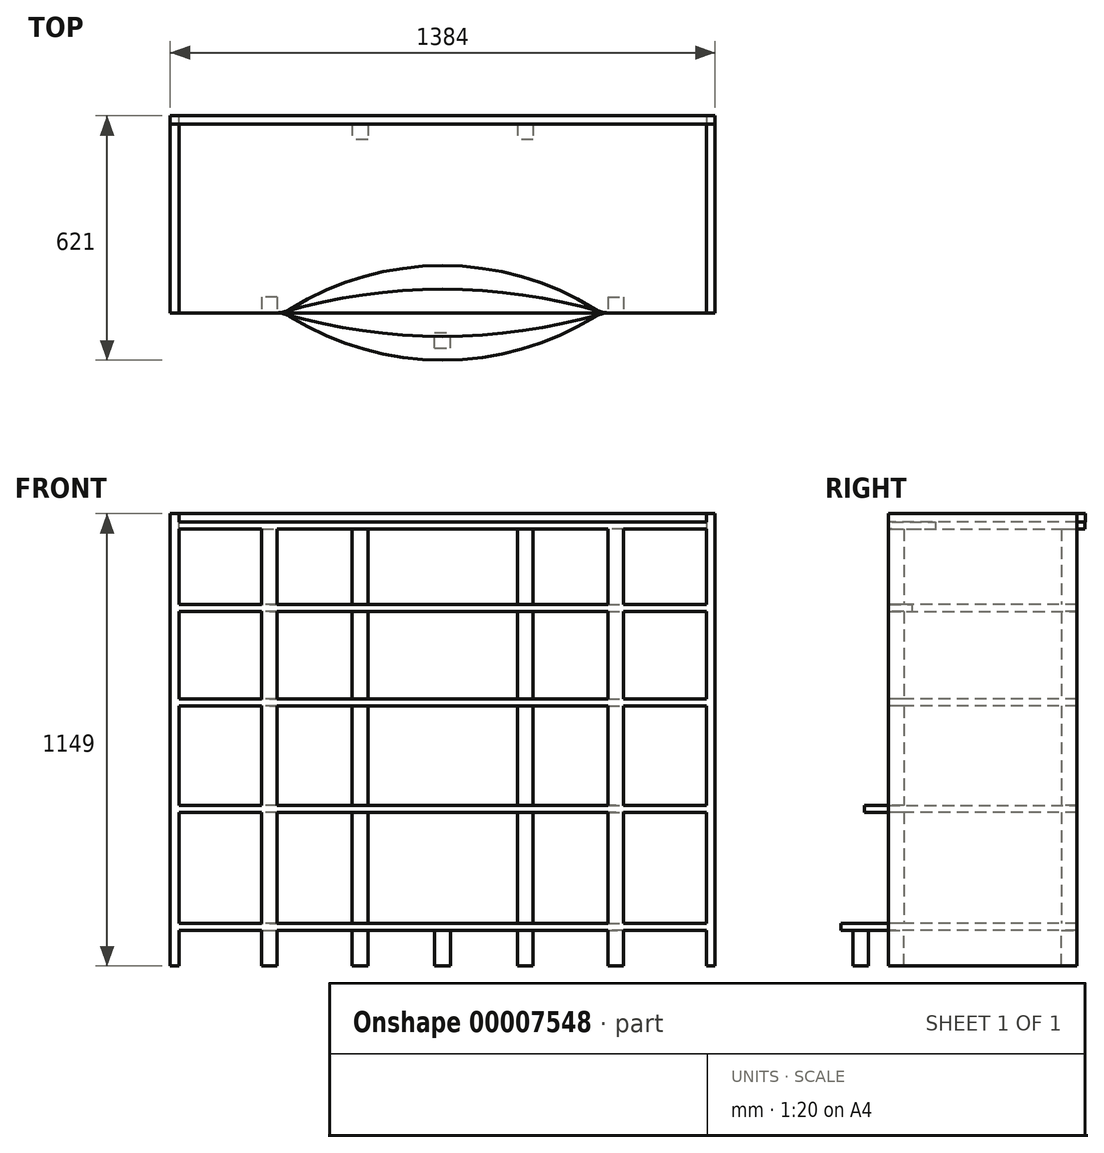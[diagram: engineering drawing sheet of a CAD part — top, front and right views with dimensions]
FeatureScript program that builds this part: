
annotation { "Feature Type Name" : "Feature", "Feature Type Description" : "" }
export const myFeature = defineFeature(function(context is Context, id is Id, definition is map)
    precondition{}
    {
        {
            var Q0;
            Q0=qCreatedBy(makeId("Top.planeOp"),FACE);
            var sketch = newSketch(context, id + "F0", { "sketchPlane" : qUnion([Q0])});
            skLineSegment(sketch, "E0", {"start": v(-670, 0) * mm, "end": v(-670, -480) * mm});
            skLineSegment(sketch, "E1", {"start": v(-670, -480) * mm, "end": v(-420, -480) * mm});
            skLineSegment(sketch, "E2", {"start": v(-670, 0) * mm, "end": v(670, 0) * mm});
            skLineSegment(sketch, "E3", {"start": v(670, 0) * mm, "end": v(670, -480) * mm});
            skLineSegment(sketch, "E4", {"start": v(670, -480) * mm, "end": v(420, -480) * mm});
            skArc(sketch, "E5", {"start": v(-388.3, -489.06) * mm, "mid": v(0, -600) * mm, "end": v(388.3, -489.06) * mm});
            skPoint(sketch, "E6.visualSharp", {"position": v(-402.5, -480) * mm});
            skArc(sketch, "E6.filletArc", {"start": v(-388.3, -489.06) * mm, "mid": v(-403.52, -482.3) * mm, "end": v(-420, -480) * mm});
            skPoint(sketch, "E7.visualSharp", {"position": v(402.5, -480) * mm});
            skArc(sketch, "E7.filletArc", {"start": v(420, -480) * mm, "mid": v(403.52, -482.3) * mm, "end": v(388.3, -489.06) * mm});
            skSolve(sketch);
        }
        {
            var Q0;
            Q0=qCreatedBy(makeId("Top.planeOp"),FACE);
            cPlane(context, id + "F1", {"entities" : qUnion([Q0]), "cplaneType" : CPlaneType.OFFSET, "offset" : 300 * mm, "width" : 150 * mm, "height" : 150 * mm});
        }
        {
            var Q0;
            Q0=qCreatedBy(id+"F1.planeOp",FACE);
            var sketch = newSketch(context, id + "F2", { "sketchPlane" : qUnion([Q0])});
            skLineSegment(sketch, "E8", {"start": v(-670, 0) * mm, "end": v(-670, -480) * mm});
            skLineSegment(sketch, "E9", {"start": v(-670, -480) * mm, "end": v(-420, -480) * mm});
            skLineSegment(sketch, "E10", {"start": v(420, -480) * mm, "end": v(670, -480) * mm});
            skLineSegment(sketch, "E11", {"start": v(670, -480) * mm, "end": v(670, 0) * mm});
            skLineSegment(sketch, "E12", {"start": v(670, 0) * mm, "end": v(-670, 0) * mm});
            skArc(sketch, "E13", {"start": v(-403.2, -482.4) * mm, "mid": v(0, -540) * mm, "end": v(403.2, -482.4) * mm});
            skPoint(sketch, "E14.visualSharp", {"position": v(-411.34, -480) * mm});
            skArc(sketch, "E14.filletArc", {"start": v(-403.2, -482.4) * mm, "mid": v(-411.51, -480.6) * mm, "end": v(-420, -480) * mm});
            skPoint(sketch, "E15.visualSharp", {"position": v(411.34, -480) * mm});
            skArc(sketch, "E15.filletArc", {"start": v(420, -480) * mm, "mid": v(411.51, -480.6) * mm, "end": v(403.2, -482.4) * mm});
            skSolve(sketch);
        }
        {
            var Q0;
            Q0=qCreatedBy(id+"F1.planeOp",FACE);
            cPlane(context, id + "F3", {"entities" : qUnion([Q0]), "cplaneType" : CPlaneType.OFFSET, "offset" : 270 * mm, "width" : 150 * mm, "height" : 150 * mm});
        }
        {
            var Q0;
            Q0=qCreatedBy(id+"F3.planeOp",FACE);
            var sketch = newSketch(context, id + "F4", { "sketchPlane" : qUnion([Q0])});
            skLineSegment(sketch, "E16.bottom", {"start": v(-670, 0) * mm, "end": v(670, 0) * mm});
            skLineSegment(sketch, "E16.top", {"start": v(-670, -480) * mm, "end": v(670, -480) * mm});
            skLineSegment(sketch, "E16.left", {"start": v(-670, 0) * mm, "end": v(-670, -480) * mm});
            skLineSegment(sketch, "E16.right", {"start": v(670, 0) * mm, "end": v(670, -480) * mm});
            skSolve(sketch);
        }
        {
            var Q0;
            Q0=qCreatedBy(id+"F3.planeOp",FACE);
            cPlane(context, id + "F5", {"entities" : qUnion([Q0]), "cplaneType" : CPlaneType.OFFSET, "offset" : 240 * mm, "width" : 150 * mm, "height" : 150 * mm});
        }
        {
            var Q0;
            Q0=qCreatedBy(id+"F5.planeOp",FACE);
            var sketch = newSketch(context, id + "F6", { "sketchPlane" : qUnion([Q0])});
            skLineSegment(sketch, "E17", {"start": v(-420, -480) * mm, "end": v(-670, -480) * mm});
            skLineSegment(sketch, "E18", {"start": v(-670, -480) * mm, "end": v(-670, 0) * mm});
            skLineSegment(sketch, "E19", {"start": v(-670, 0) * mm, "end": v(670, 0) * mm});
            skLineSegment(sketch, "E20", {"start": v(670, 0) * mm, "end": v(670, -480) * mm});
            skLineSegment(sketch, "E21", {"start": v(670, -480) * mm, "end": v(420, -480) * mm});
            skArc(sketch, "E22", {"start": v(403.2, -477.6) * mm, "mid": v(0, -420) * mm, "end": v(-403.2, -477.6) * mm});
            skPoint(sketch, "E23.visualSharp", {"position": v(-411.34, -480) * mm});
            skArc(sketch, "E23.filletArc", {"start": v(-420, -480) * mm, "mid": v(-411.51, -479.4) * mm, "end": v(-403.2, -477.6) * mm});
            skPoint(sketch, "E24.visualSharp", {"position": v(411.34, -480) * mm});
            skArc(sketch, "E24.filletArc", {"start": v(403.2, -477.6) * mm, "mid": v(411.51, -479.4) * mm, "end": v(420, -480) * mm});
            skSolve(sketch);
        }
        {
            var Q0;
            Q0=qCreatedBy(id+"F5.planeOp",FACE);
            cPlane(context, id + "F7", {"entities" : qUnion([Q0]), "cplaneType" : CPlaneType.OFFSET, "offset" : 210 * mm, "width" : 150 * mm, "height" : 150 * mm});
        }
        {
            var Q0;
            Q0=qCreatedBy(id+"F7.planeOp",FACE);
            var sketch = newSketch(context, id + "F8", { "sketchPlane" : qUnion([Q0])});
            skLineSegment(sketch, "E25", {"start": v(-420, -480) * mm, "end": v(-670, -480) * mm});
            skLineSegment(sketch, "E26", {"start": v(-670, -480) * mm, "end": v(-670, 0) * mm});
            skLineSegment(sketch, "E27", {"start": v(670, 0) * mm, "end": v(670, -480) * mm});
            skLineSegment(sketch, "E28", {"start": v(670, -480) * mm, "end": v(420, -480) * mm});
            skArc(sketch, "E29", {"start": v(388.3, -470.94) * mm, "mid": v(0, -360) * mm, "end": v(-388.3, -470.94) * mm});
            skPoint(sketch, "E30.visualSharp", {"position": v(-402.5, -480) * mm});
            skArc(sketch, "E30.filletArc", {"start": v(-420, -480) * mm, "mid": v(-403.52, -477.7) * mm, "end": v(-388.3, -470.94) * mm});
            skPoint(sketch, "E31.visualSharp", {"position": v(402.5, -480) * mm});
            skArc(sketch, "E31.filletArc", {"start": v(388.3, -470.94) * mm, "mid": v(403.52, -477.7) * mm, "end": v(420, -480) * mm});
            skLineSegment(sketch, "E32", {"start": v(-670, 0) * mm, "end": v(-670, 20) * mm});
            skLineSegment(sketch, "E33", {"start": v(-670, 20) * mm, "end": v(670, 20) * mm});
            skLineSegment(sketch, "E34", {"start": v(670, 20) * mm, "end": v(670, 0) * mm});
            skSolve(sketch);
        }
        {
            var Q0;
            Q0 = qSketchRegion(id + "F4", true);
            var Q1;
            Q1 = qSketchRegion(id + "F2", true);
            var Q2;
            Q2 = qSketchRegion(id + "F0", true);
            var Q3;
            Q3 = qSketchRegion(id + "F6", true);
            var Q4;
            Q4 = qSketchRegion(id + "F8", true);
            extrude(context, id + "F9", {"entities" : qUnion([Q0, Q1, Q2, Q3, Q4]), "depth" : 18 * mm});
        }
        {
            var Q0;
            Q0=makeQuery(id+"F9.opExtrude","SWEPT_FACE",FACE,{"disambiguationData":[OSD([sQuery(id+"F8.wireOp",EDGE,"E27")])]});
            var sketch = newSketch(context, id + "F10", { "sketchPlane" : qUnion([Q0])});
            skLineSegment(sketch, "E35.bottom", {"start": v(-480, 1059) * mm, "end": v(0, 1059) * mm});
            skLineSegment(sketch, "E35.top", {"start": v(-480, 0) * mm, "end": v(0, 0) * mm});
            skLineSegment(sketch, "E35.left", {"start": v(-480, 1059) * mm, "end": v(-480, 0) * mm});
            skLineSegment(sketch, "E35.right", {"start": v(0, 1059) * mm, "end": v(0, 0) * mm});
            skSolve(sketch);
        }
        {
            var Q0;
            Q0 = qSketchRegion(id + "F10", true);
            extrude(context, id + "F11", {"entities" : qUnion([Q0]), "operationType" : NewBodyOperationType.ADD, "depth" : 22 * mm});
        }
        {
            var Q0;
            Q0=makeQuery(id+"F9.opExtrude","SWEPT_FACE",FACE,{"disambiguationData":[OSD([sQuery(id+"F8.wireOp",EDGE,"E26")])]});
            var sketch = newSketch(context, id + "F12", { "sketchPlane" : qUnion([Q0])});
            skLineSegment(sketch, "E36.bottom", {"start": v(480, 1038) * mm, "end": v(480, 1038) * mm});
            skLineSegment(sketch, "E36.top", {"start": v(480, 0) * mm, "end": v(480, 0) * mm});
            skLineSegment(sketch, "E36.left", {"start": v(480, 1038) * mm, "end": v(480, 0) * mm});
            skLineSegment(sketch, "E36.right", {"start": v(480, 1038) * mm, "end": v(480, 0) * mm});
            skLineSegment(sketch, "E37", {"start": v(480, 0) * mm, "end": v(0, 0) * mm});
            skLineSegment(sketch, "E38", {"start": v(0, 0) * mm, "end": v(0, 1038) * mm});
            skLineSegment(sketch, "E39", {"start": v(0, 1038) * mm, "end": v(480, 1038) * mm, "construction": true});
            skLineSegment(sketch, "E40", {"start": v(0, 1038) * mm, "end": v(0, 1059) * mm});
            skLineSegment(sketch, "E41", {"start": v(0, 1059) * mm, "end": v(480, 1059) * mm});
            skLineSegment(sketch, "E42", {"start": v(480, 1059) * mm, "end": v(480, 1038) * mm});
            skSolve(sketch);
        }
        {
            var Q0;
            Q0 = qSketchRegion(id + "F12", true);
            extrude(context, id + "F13", {"entities" : qUnion([Q0]), "operationType" : NewBodyOperationType.ADD, "depth" : 22 * mm});
        }
        {
            var Q0;
            Q0=makeQuery(id+"F0.imprint","IMPRINT",FACE,{"disambiguationData":[TD([[makeQuery(id+"F0.imprint","IMPRINT",EDGE,{"derivedFrom":sQuery(id+"F0.wireOp",EDGE,"E0")}),1.0]])]});
            var sketch = newSketch(context, id + "F14", { "sketchPlane" : qUnion([Q0])});
            skLineSegment(sketch, "E43.bottom", {"start": v(-692, 0) * mm, "end": v(-670, 0) * mm});
            skLineSegment(sketch, "E43.top", {"start": v(-692, -480) * mm, "end": v(-670, -480) * mm});
            skLineSegment(sketch, "E43.left", {"start": v(-692, 0) * mm, "end": v(-692, -480) * mm});
            skLineSegment(sketch, "E43.right", {"start": v(-670, 0) * mm, "end": v(-670, -480) * mm});
            skLineSegment(sketch, "E44.bottom", {"start": v(-460, -480) * mm, "end": v(-420, -480) * mm});
            skLineSegment(sketch, "E44.top", {"start": v(-460, -440) * mm, "end": v(-420, -440) * mm});
            skLineSegment(sketch, "E44.left", {"start": v(-460, -480) * mm, "end": v(-460, -440) * mm});
            skLineSegment(sketch, "E44.right", {"start": v(-420, -480) * mm, "end": v(-420, -440) * mm});
            skLineSegment(sketch, "E45.bottom", {"start": v(-230, -40) * mm, "end": v(-190, -40) * mm});
            skLineSegment(sketch, "E45.top", {"start": v(-230, 0) * mm, "end": v(-190, 0) * mm});
            skLineSegment(sketch, "E45.left", {"start": v(-230, -40) * mm, "end": v(-230, 0) * mm});
            skLineSegment(sketch, "E45.right", {"start": v(-190, -40) * mm, "end": v(-190, 0) * mm});
            skLineSegment(sketch, "E46.bottom", {"start": v(190, -40) * mm, "end": v(230, -40) * mm});
            skLineSegment(sketch, "E46.top", {"start": v(190, 0) * mm, "end": v(230, 0) * mm});
            skLineSegment(sketch, "E46.left", {"start": v(190, -40) * mm, "end": v(190, 0) * mm});
            skLineSegment(sketch, "E46.right", {"start": v(230, -40) * mm, "end": v(230, 0) * mm});
            skLineSegment(sketch, "E47.bottom", {"start": v(460, -480) * mm, "end": v(420, -480) * mm});
            skLineSegment(sketch, "E47.top", {"start": v(460, -440) * mm, "end": v(420, -440) * mm});
            skLineSegment(sketch, "E47.left", {"start": v(460, -480) * mm, "end": v(460, -440) * mm});
            skLineSegment(sketch, "E47.right", {"start": v(420, -480) * mm, "end": v(420, -440) * mm});
            skLineSegment(sketch, "E48.bottom", {"start": v(692, -480) * mm, "end": v(670, -480) * mm});
            skLineSegment(sketch, "E48.top", {"start": v(692, 0) * mm, "end": v(670, 0) * mm});
            skLineSegment(sketch, "E48.left", {"start": v(692, -480) * mm, "end": v(692, 0) * mm});
            skLineSegment(sketch, "E48.right", {"start": v(670, -480) * mm, "end": v(670, 0) * mm});
            skLineSegment(sketch, "E49.bottom", {"start": v(-20, -570) * mm, "end": v(20, -570) * mm});
            skLineSegment(sketch, "E49.top", {"start": v(-20, -530) * mm, "end": v(20, -530) * mm});
            skLineSegment(sketch, "E49.left", {"start": v(-20, -570) * mm, "end": v(-20, -530) * mm});
            skLineSegment(sketch, "E49.right", {"start": v(20, -570) * mm, "end": v(20, -530) * mm});
            skSolve(sketch);
        }
        {
            var Q0;
            Q0 = qSketchRegion(id + "F14", true);
            extrude(context, id + "F15", {"entities" : qUnion([Q0]), "operationType" : NewBodyOperationType.ADD, "oppositeDirection" : true, "depth" : 90 * mm});
        }
        {
            var Q0;
            Q0=makeQuery(id+"F14.imprint","IMPRINT",FACE,{"disambiguationData":[TD([[makeQuery(id+"F14.imprint","IMPRINT",EDGE,{"derivedFrom":sQuery(id+"F14.wireOp",EDGE,"E44.top")}),-1.0]])]});
            var Q1;
            Q1=makeQuery(id+"F14.imprint","IMPRINT",FACE,{"disambiguationData":[TD([[makeQuery(id+"F14.imprint","IMPRINT",EDGE,{"derivedFrom":sQuery(id+"F14.wireOp",EDGE,"E47.top")}),1.0]])]});
            var Q2;
            Q2=makeQuery(id+"F14.imprint","IMPRINT",FACE,{"disambiguationData":[TD([[makeQuery(id+"F14.imprint","IMPRINT",EDGE,{"derivedFrom":sQuery(id+"F14.wireOp",EDGE,"E46.bottom")}),1.0]])]});
            var Q3;
            Q3=makeQuery(id+"F14.imprint","IMPRINT",FACE,{"disambiguationData":[TD([[makeQuery(id+"F14.imprint","IMPRINT",EDGE,{"derivedFrom":sQuery(id+"F14.wireOp",EDGE,"E45.bottom")}),1.0]])]});
            var Q4;
            Q4=qCreatedBy(id+"F7.planeOp",FACE);
            extrude(context, id + "F16", {"entities" : qUnion([Q0, Q1, Q2, Q3]), "operationType" : NewBodyOperationType.ADD, "endBound" : BoundingType.UP_TO_SURFACE, "endBoundEntityFace" : qUnion([Q4]), "depth" : 1200 * mm});
        }
        {
            var Q0;
            Q0=makeQuery(id+"F15.boolean.opBoolean","MERGE",FACE,{"derivedFrom":[makeQuery(id+"F11.opExtrude","CAP_FACE",FACE,{"disambiguationData":[OSD([sQuery(id+"F10.wireOp",EDGE,"E35.bottom"),sQuery(id+"F10.wireOp",EDGE,"E35.top"),sQuery(id+"F10.wireOp",EDGE,"E35.left"),sQuery(id+"F10.wireOp",EDGE,"E35.right")])],"isStart":false}),makeQuery(id+"F15.opExtrude","SWEPT_FACE",FACE,{"disambiguationData":[OSD([sQuery(id+"F14.wireOp",EDGE,"E48.left")])]})]});
            var sketch = newSketch(context, id + "F17", { "sketchPlane" : qUnion([Q0])});
            skLineSegment(sketch, "E50.bottom", {"start": v(0, 1059) * mm, "end": v(21, 1059) * mm});
            skLineSegment(sketch, "E50.top", {"start": v(0, 1038) * mm, "end": v(21, 1038) * mm});
            skLineSegment(sketch, "E50.left", {"start": v(0, 1059) * mm, "end": v(0, 1038) * mm});
            skLineSegment(sketch, "E50.right", {"start": v(21, 1059) * mm, "end": v(21, 1038) * mm});
            skSolve(sketch);
        }
        {
            var Q0;
            Q0=makeQuery(id+"F17.imprint","IMPRINT",FACE,{"disambiguationData":[TD([[makeQuery(id+"F17.imprint","IMPRINT",EDGE,{"derivedFrom":sQuery(id+"F17.wireOp",EDGE,"E50.bottom")}),-1.0]])]});
            var Q1;
            Q1=makeQuery(id+"F15.boolean.opBoolean","MERGE",FACE,{"derivedFrom":[makeQuery(id+"F13.opExtrude","CAP_FACE",FACE,{"disambiguationData":[OSD([sQuery(id+"F12.wireOp",EDGE,"E36.right"),sQuery(id+"F12.wireOp",EDGE,"E37"),sQuery(id+"F12.wireOp",EDGE,"E38"),sQuery(id+"F12.wireOp",EDGE,"E40"),sQuery(id+"F12.wireOp",EDGE,"E41"),sQuery(id+"F12.wireOp",EDGE,"E42")])],"isStart":false}),makeQuery(id+"F15.opExtrude","SWEPT_FACE",FACE,{"disambiguationData":[OSD([sQuery(id+"F14.wireOp",EDGE,"E43.left")])]})]});
            extrude(context, id + "F18", {"entities" : qUnion([Q0]), "endBound" : BoundingType.UP_TO_SURFACE, "oppositeDirection" : true, "endBoundEntityFace" : qUnion([Q1]), "depth" : 25 * mm});
        }
    });
